# Revit family: P560260-028-30
name_source: partatom
category: Lighting Fixtures
revit_build: Autodesk Revit 2014 (Build: 20130308_1515(x64)
units: mm (PartAtom-declared; Revit-internal decimal feet)

## types (1)
- P560260-028-30
    Apparent Load = 9 VA
    Color Filter = 16777215
    Connector Description = Lighting Connector
    Default Elevation = 48 "
    Description = Function follows form in the Z-2020 LED Collection 1-Light Satin White LED Modern Outdoor Round Wall Light. The circular shade is coated in a crisp satin white finish. The LED light casts around the edges of the shade creating a glow reminiscent of a total eclipse.
    Dimming Lamp Color Temperature Shift = <None>
    Features = Application: Function follows form in the Z-2020 LED Collection 1-Light Satin White LED Modern Outdoor Round Wall Light ideal for any covered porch, patio, deck, entryway, hallway, foyer, bedroom, sitting room, or bathroom.
Styles: Perfect for modern and contemporary style settings.
Finish: The circular shade is coated in a crisp satin white finish.
Materials: Constructed from aluminum to ensure a long product lifespan.
Glass/Shades: The LED light casts around the edges of the shade creating a glow reminiscent of a total eclipse.
Bulbs: For ideal illumination, 1 LED module is included (9w)
3000K
90CRI
623 delivered lumens
dimmable.
Dimensions: Measures 6-1/4-inch diameter by 2-1/4-inch height.
Certifications: cCSAus wet location listed, ENERGY STAR qualified, meets California Title 24 JA8-2016.
Pairs With: Pairs with a variety of Progress Lighting fixtures.
Warranty: Our 5-Year Limited Warranty guarantees your complete satisfaction with your purchase and includes professional after-sales customer service support.
    Fixture distribution = Direct
    Glass = Paint - Hubbell - White Texture
    Gold = Hubbell Metal Brass
    Housing Material = Paint - Hubbell - Matte White
    Lamp = LED
    Load Classification = Lighting
    Manufacturer = Progress Lighting
    Model = P560260-028-30
    Photometric Web File = generic.ies
    Power Factor = 1
    Product Documentation Link = https://hubbellcdn.com
    Product Link = https://www.hubbell.com
    Support = Paint - Hubbell - Light Silver
    Tilt Angle = -90.00°
    URL = https://www.hubbell.com
    Voltage = 120 V
    Warranty = 5 year Warranty
    Wattage Comments = 9W
    Watts = 9 W

## geometry (parser evidence)
native form markers: Sweep x4
no freeform markers — native parametric forms only
